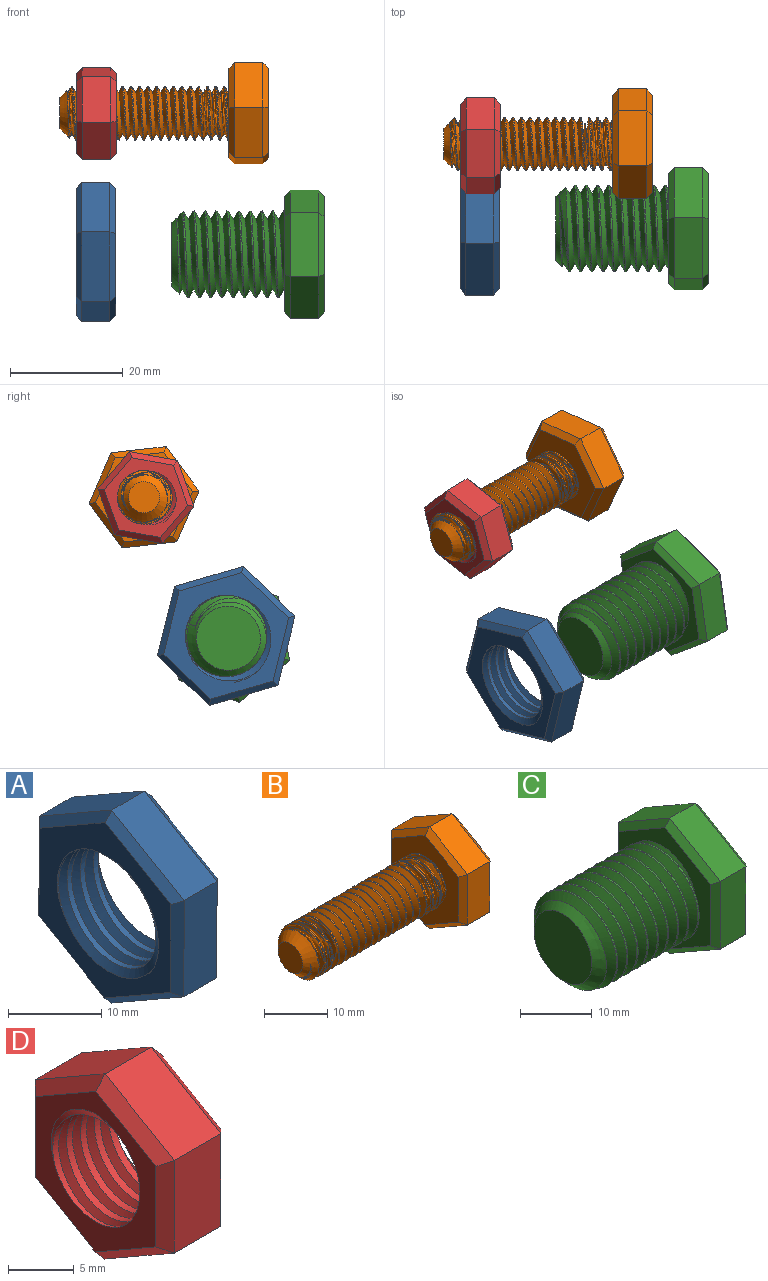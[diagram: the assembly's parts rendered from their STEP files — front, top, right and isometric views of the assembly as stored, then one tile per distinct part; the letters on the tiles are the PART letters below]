
ASSEMBLY  parts=4 mates=2
PART A: 23 faces, bbox 9.3x22.7x26 mm
  f0: cylinder r=7.24mm len=14.48mm, axis (1,0,0), area 111.6mm2, adj f7,f8,f21,f22
  f1: plane 10.98x6.38mm, normal (0,-0.5,0.86), area 63.5mm2, adj f2,f6,f14,f18
  f2: plane 12.7x5mm, normal (0,-1,0), area 63.5mm2, adj f1,f3,f12,f16
  f3: plane 11.02x6.32mm, normal (0,-0.5,-0.87), area 63.5mm2, adj f2,f4,f10,f15
  f4: plane 10.98x6.38mm, normal (0,0.5,-0.86), area 63.5mm2, adj f3,f5,f9,f17
  f5: plane 12.7x5mm, normal (0,1,0), area 63.5mm2, adj f4,f6,f11,f19
  f6: plane 11.02x6.32mm, normal (0,0.5,0.87), area 63.5mm2, adj f1,f5,f13,f20
  f7: plane 23.73x20.67mm, normal (-1,0,0), area 164.4mm2, adj f0,f9,f10,f11,f12,f13,f14,f21
  f8: plane 23.73x20.67mm, normal (1,0,0), area 164.4mm2, adj f0,f15,f16,f17,f18,f19,f20,f21
  f9: plane 10.99x6.96mm, normal (-0.71,0.36,-0.61), area 17.1mm2, adj f4,f7,f10,f11
  f10: plane 11.02x6.9mm, normal (-0.71,-0.35,-0.61), area 17.1mm2, adj f3,f7,f9,f12
  f11: plane 12.7x1.03mm, normal (-0.71,0.71,0), area 17.1mm2, adj f5,f7,f9,f13
  f12: plane 12.7x1.03mm, normal (-0.71,-0.71,0), area 17.1mm2, adj f2,f7,f10,f14
  f13: plane 11.02x6.9mm, normal (-0.71,0.35,0.61), area 17.1mm2, adj f6,f7,f11,f14
  f14: plane 10.99x6.96mm, normal (-0.71,-0.36,0.61), area 17.1mm2, adj f1,f7,f12,f13
  f15: plane 11.02x6.9mm, normal (0.71,-0.35,-0.61), area 17.1mm2, adj f3,f8,f16,f17
  f16: plane 12.7x1.03mm, normal (0.71,-0.71,0), area 17.1mm2, adj f2,f8,f15,f18
  f17: plane 10.99x6.96mm, normal (0.71,0.36,-0.61), area 17.1mm2, adj f4,f8,f15,f19
  f18: plane 10.99x6.96mm, normal (0.71,-0.36,0.61), area 17.1mm2, adj f1,f8,f16,f20
  f19: plane 12.7x1.03mm, normal (0.71,0.71,0), area 17.1mm2, adj f5,f8,f17,f20
  f20: plane 11.02x6.9mm, normal (0.71,0.35,0.61), area 17.1mm2, adj f6,f8,f18,f19
  f21: bspline ~19.31x16.73mm, area 223mm2, adj f0,f7,f8,f22
  f22: bspline ~19.31x16.73mm, area 223mm2, adj f0,f7,f8,f21
PART B: 26 faces, bbox 37.8x17.9x20.5 mm
  f0: cylinder r=4.75mm len=28mm, axis (1,0,0), area 17mm2, adj f1,f2,f4,f5,f13
  f1: bspline ~30.66x10.97mm, area 656.5mm2, adj f0,f2,f4,f13
  f2: bspline ~30.16x10.97mm, area 658mm2, adj f0,f1,f4,f5,f13
  f3: plane 5.5x5.5mm, normal (-1,0,0), area 23.8mm2, adj f4
  f4: cone r=4.75mm half-angle=45deg, axis (1,0,0), area 47mm2, adj f0,f1,f2,f3,f5
  f5: cone r=4.75mm half-angle=45deg, axis (1,0,0), area 0.3mm2, adj f0,f2,f4
  f6: plane 8.52x5mm, normal (0,0.5,0.87), area 49.1mm2, adj f7,f11,f18,f25
  f7: plane 8.48x5mm, normal (0,-0.5,0.86), area 49.1mm2, adj f6,f8,f19,f23
  f8: plane 9.82x5mm, normal (0,-1,0), area 49.1mm2, adj f7,f9,f17,f21
  f9: plane 8.52x5mm, normal (0,-0.5,-0.87), area 49.1mm2, adj f8,f10,f15,f20
  f10: plane 8.48x5mm, normal (0,0.5,-0.86), area 49.1mm2, adj f9,f11,f14,f22
  f11: plane 9.82x5mm, normal (0,1,0), area 49.1mm2, adj f6,f10,f16,f24
  f12: plane 17.32x15.03mm, normal (1,0,0), area 194.9mm2, adj f14,f15,f16,f17,f18,f19
  f13: plane 18.14x15.85mm, normal (-1,0,0), area 137.6mm2, adj f0,f1,f2,f20,f21,f22,f23,f24
  f14: plane 8.49x5.51mm, normal (0.71,0.36,-0.61), area 13.1mm2, adj f10,f12,f15,f16
  f15: plane 8.52x5.46mm, normal (0.71,-0.35,-0.61), area 13.1mm2, adj f9,f12,f14,f17
  f16: plane 9.82x1.03mm, normal (0.71,0.71,0), area 13.1mm2, adj f11,f12,f14,f18
  f17: plane 9.82x1.03mm, normal (0.71,-0.71,0), area 13.1mm2, adj f8,f12,f15,f19
  f18: plane 8.52x5.46mm, normal (0.71,0.35,0.61), area 13.1mm2, adj f6,f12,f16,f19
  f19: plane 8.49x5.51mm, normal (0.71,-0.36,0.61), area 13.1mm2, adj f7,f12,f17,f18
  f20: plane 8.52x5.46mm, normal (-0.71,-0.35,-0.61), area 13.1mm2, adj f9,f13,f21,f22
  f21: plane 9.82x1.03mm, normal (-0.71,-0.71,0), area 13.1mm2, adj f8,f13,f20,f23
  f22: plane 8.49x5.51mm, normal (-0.71,0.36,-0.61), area 13.1mm2, adj f10,f13,f20,f24
  f23: plane 8.49x5.51mm, normal (-0.71,-0.36,0.61), area 13.1mm2, adj f7,f13,f21,f25
  f24: plane 9.82x1.03mm, normal (-0.71,0.71,0), area 13.1mm2, adj f11,f13,f22,f25
  f25: plane 8.52x5.46mm, normal (-0.71,0.35,0.61), area 13.1mm2, adj f6,f13,f23,f24
PART C: 26 faces, bbox 27.7x20x23.1 mm
  f0: cylinder r=7.68mm len=18mm, axis (1,0,0), area 139.1mm2, adj f1,f2,f5,f13
  f1: bspline ~20.88x17.74mm, area 713.8mm2, adj f0,f2,f4,f5,f13
  f2: bspline ~21.88x17.74mm, area 715.1mm2, adj f0,f1,f4,f5,f13
  f3: plane 11.36x11.36mm, normal (-1,0,0), area 101.4mm2, adj f4
  f4: cone r=7.68mm half-angle=45deg, axis (1,0,0), area 63.2mm2, adj f1,f2,f3,f5
  f5: cone r=7.68mm half-angle=45deg, axis (1,0,0), area 13.2mm2, adj f0,f1,f2,f4
  f6: plane 9.98x5.81mm, normal (0,-0.5,0.86), area 57.7mm2, adj f7,f11,f19,f23
  f7: plane 11.55x5mm, normal (0,-1,0), area 57.7mm2, adj f6,f8,f17,f21
  f8: plane 10.02x5.74mm, normal (0,-0.5,-0.87), area 57.7mm2, adj f7,f9,f15,f20
  f9: plane 9.98x5.81mm, normal (0,0.5,-0.86), area 57.7mm2, adj f8,f10,f14,f22
  f10: plane 11.55x5mm, normal (0,1,0), area 57.7mm2, adj f9,f11,f16,f24
  f11: plane 10.02x5.74mm, normal (0,0.5,0.87), area 57.7mm2, adj f6,f10,f18,f25
  f12: plane 20.78x18.04mm, normal (1,0,0), area 280.6mm2, adj f14,f15,f16,f17,f18,f19
  f13: plane 20.78x18.04mm, normal (-1,0,0), area 125.2mm2, adj f0,f1,f2,f20,f21,f22,f23,f24
  f14: plane 9.98x6.38mm, normal (0.71,0.36,-0.61), area 15.5mm2, adj f9,f12,f15,f16
  f15: plane 10.02x6.32mm, normal (0.71,-0.35,-0.61), area 15.5mm2, adj f8,f12,f14,f17
  f16: plane 11.55x1.04mm, normal (0.71,0.71,0), area 15.5mm2, adj f10,f12,f14,f18
  f17: plane 11.55x1.04mm, normal (0.71,-0.71,0), area 15.5mm2, adj f7,f12,f15,f19
  f18: plane 10.02x6.32mm, normal (0.71,0.35,0.61), area 15.5mm2, adj f11,f12,f16,f19
  f19: plane 9.98x6.38mm, normal (0.71,-0.36,0.61), area 15.5mm2, adj f6,f12,f17,f18
  f20: plane 10.02x6.32mm, normal (-0.71,-0.35,-0.61), area 15.5mm2, adj f8,f13,f21,f22
  f21: plane 11.55x1.04mm, normal (-0.71,-0.71,0), area 15.5mm2, adj f7,f13,f20,f23
  f22: plane 9.98x6.38mm, normal (-0.71,0.36,-0.61), area 15.5mm2, adj f9,f13,f20,f24
  f23: plane 9.98x6.38mm, normal (-0.71,-0.36,0.61), area 15.5mm2, adj f6,f13,f21,f25
  f24: plane 11.55x1.04mm, normal (-0.71,0.71,0), area 15.5mm2, adj f10,f13,f22,f25
  f25: plane 10.02x6.32mm, normal (-0.71,0.35,0.61), area 15.5mm2, adj f11,f13,f23,f24
PART D: 23 faces, bbox 9.1x15.4x17.7 mm
  f0: plane 7.49x5mm, normal (0,-0.5,0.86), area 43.3mm2, adj f1,f5,f13,f17
  f1: plane 8.66x5mm, normal (0,-1,0), area 43.3mm2, adj f0,f2,f11,f15
  f2: plane 7.51x5mm, normal (0,-0.5,-0.87), area 43.3mm2, adj f1,f3,f9,f14
  f3: plane 7.49x5mm, normal (0,0.5,-0.86), area 43.3mm2, adj f2,f4,f8,f16
  f4: plane 8.66x5mm, normal (0,1,0), area 43.3mm2, adj f3,f5,f10,f18
  f5: plane 7.51x5mm, normal (0,0.5,0.87), area 43.3mm2, adj f0,f4,f12,f19
  f6: plane 15.37x13.38mm, normal (-1,0,0), area 71.4mm2, adj f8,f9,f10,f11,f12,f13,f20,f21
  f7: plane 15.37x13.38mm, normal (1,0,0), area 71.4mm2, adj f14,f15,f16,f17,f18,f19,f20,f21
  f8: plane 7.49x4.93mm, normal (-0.71,0.36,-0.61), area 11.4mm2, adj f3,f6,f9,f10
  f9: plane 7.51x4.89mm, normal (-0.71,-0.35,-0.61), area 11.4mm2, adj f2,f6,f8,f11
  f10: plane 8.66x1.02mm, normal (-0.71,0.71,0), area 11.4mm2, adj f4,f6,f8,f12
  f11: plane 8.66x1.02mm, normal (-0.71,-0.71,0), area 11.4mm2, adj f1,f6,f9,f13
  f12: plane 7.51x4.89mm, normal (-0.71,0.35,0.61), area 11.4mm2, adj f5,f6,f10,f13
  f13: plane 7.49x4.93mm, normal (-0.71,-0.36,0.61), area 11.4mm2, adj f0,f6,f11,f12
  f14: plane 7.51x4.89mm, normal (0.71,-0.35,-0.61), area 11.4mm2, adj f2,f7,f15,f16
  f15: plane 8.66x1.02mm, normal (0.71,-0.71,0), area 11.4mm2, adj f1,f7,f14,f17
  f16: plane 7.49x4.93mm, normal (0.71,0.36,-0.61), area 11.4mm2, adj f3,f7,f14,f18
  f17: plane 7.49x4.93mm, normal (0.71,-0.36,0.61), area 11.4mm2, adj f0,f7,f15,f19
  f18: plane 8.66x1.02mm, normal (0.71,0.71,0), area 11.4mm2, adj f4,f7,f16,f19
  f19: plane 7.51x4.89mm, normal (0.71,0.35,0.61), area 11.4mm2, adj f5,f7,f17,f18
  f20: cylinder r=4.66mm len=9.32mm, axis (1,0,0), area 85.4mm2, adj f6,f7,f21,f22
  f21: bspline ~12.5x10.82mm, area 128.4mm2, adj f6,f7,f20,f22
  f22: bspline ~12.5x10.82mm, area 128.5mm2, adj f6,f7,f20,f21
PLACE A rot(axis=(0,0.6,-0.8),180deg) t=(-55.27,-6.86,23.48)mm fixed
PLACE B rot(axis=(1,0,0),143.4deg) t=(-24.66,7.73,48.08)mm
PLACE C rot(axis=(1,0,0),109.9deg) t=(-14.77,-7.25,23.06)mm
PLACE D rot(axis=(1,0,0),100.2deg) t=(-48.16,7.38,48.02)mm fixed
MATE cylindrical C.f0 <-> A.f7  axis (-1,0,0) through (-38.27,-7.25,23.06)mm
MATE cylindrical B.f0 <-> D.f6  axis (-1,0,0) through (-58.16,7.73,48.08)mm
